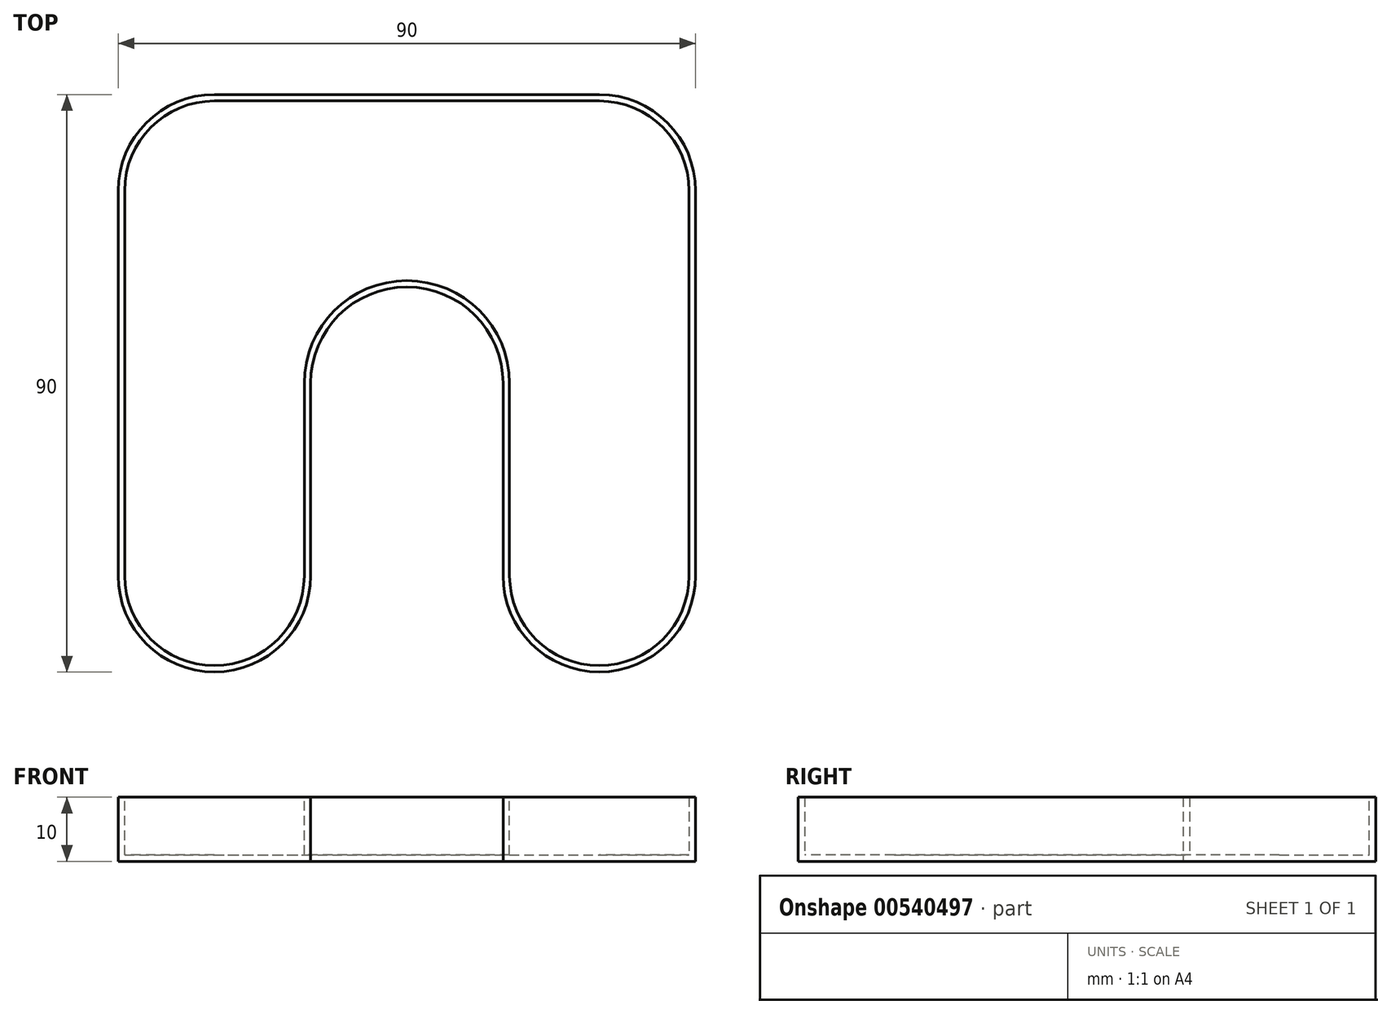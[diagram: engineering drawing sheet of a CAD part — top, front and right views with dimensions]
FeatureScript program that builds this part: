
annotation { "Feature Type Name" : "Feature", "Feature Type Description" : "" }
export const myFeature = defineFeature(function(context is Context, id is Id, definition is map)
    precondition{}
    {
        {
            var Q0;
            Q0=qCreatedBy(makeId("Top.planeOp"),FACE);
            var sketch = newSketch(context, id + "F0", { "sketchPlane" : qUnion([Q0])});
            skLineSegment(sketch, "E0", {"start": v(-29.25, 50.56) * mm, "end": v(30.75, 50.56) * mm});
            skLineSegment(sketch, "E1", {"start": v(45.75, 35.56) * mm, "end": v(45.75, -24.44) * mm});
            skLineSegment(sketch, "E2", {"start": v(30.75, -39.44) * mm, "end": v(30.75, -39.44) * mm});
            skLineSegment(sketch, "E3", {"start": v(15.75, -24.44) * mm, "end": v(15.75, 5.56) * mm});
            skLineSegment(sketch, "E4", {"start": v(0.75, 20.56) * mm, "end": v(0.75, 20.56) * mm});
            skLineSegment(sketch, "E5", {"start": v(-14.25, 5.56) * mm, "end": v(-14.25, -24.44) * mm});
            skLineSegment(sketch, "E6", {"start": v(-29.25, -39.44) * mm, "end": v(-29.25, -39.44) * mm});
            skLineSegment(sketch, "E7", {"start": v(-44.25, -24.44) * mm, "end": v(-44.25, 35.56) * mm});
            skPoint(sketch, "E8.visualSharp", {"position": v(-44.25, 50.56) * mm});
            skArc(sketch, "E8.filletArc", {"start": v(-29.25, 50.56) * mm, "mid": v(-39.86, 46.17) * mm, "end": v(-44.25, 35.56) * mm});
            skPoint(sketch, "E9.visualSharp", {"position": v(-14.25, 20.56) * mm});
            skArc(sketch, "E9.filletArc", {"start": v(0.75, 20.56) * mm, "mid": v(-9.86, 16.17) * mm, "end": v(-14.25, 5.56) * mm});
            skPoint(sketch, "E10.visualSharp", {"position": v(15.75, 20.56) * mm});
            skArc(sketch, "E10.filletArc", {"start": v(15.75, 5.56) * mm, "mid": v(11.35, 16.17) * mm, "end": v(0.75, 20.56) * mm});
            skPoint(sketch, "E11.visualSharp", {"position": v(45.75, 50.56) * mm});
            skArc(sketch, "E11.filletArc", {"start": v(45.75, 35.56) * mm, "mid": v(41.35, 46.17) * mm, "end": v(30.75, 50.56) * mm});
            skPoint(sketch, "E12.visualSharp", {"position": v(15.75, -39.44) * mm});
            skArc(sketch, "E12.filletArc", {"start": v(15.75, -24.44) * mm, "mid": v(20.14, -35.05) * mm, "end": v(30.75, -39.44) * mm});
            skPoint(sketch, "E13.visualSharp", {"position": v(45.75, -39.44) * mm});
            skArc(sketch, "E13.filletArc", {"start": v(30.75, -39.44) * mm, "mid": v(41.35, -35.05) * mm, "end": v(45.75, -24.44) * mm});
            skPoint(sketch, "E14.visualSharp", {"position": v(-14.25, -39.44) * mm});
            skArc(sketch, "E14.filletArc", {"start": v(-29.25, -39.44) * mm, "mid": v(-18.65, -35.05) * mm, "end": v(-14.25, -24.44) * mm});
            skPoint(sketch, "E15.visualSharp", {"position": v(-44.25, -39.44) * mm});
            skArc(sketch, "E15.filletArc", {"start": v(-44.25, -24.44) * mm, "mid": v(-39.86, -35.05) * mm, "end": v(-29.25, -39.44) * mm});
            skSolve(sketch);
        }
        {
            var Q0;
            Q0=makeQuery(id+"F0.imprint","IMPRINT",FACE,{"disambiguationData":[TD([[makeQuery(id+"F0.imprint","IMPRINT",EDGE,{"derivedFrom":sQuery(id+"F0.wireOp",EDGE,"E0")}),-1.0]])]});
            extrude(context, id + "F1", {"entities" : qUnion([Q0]), "depth" : 10 * mm, "offsetDistance" : 25 * mm});
        }
        {
            var Q0;
            Q0=makeQuery(id+"F1.opExtrude","CAP_FACE",FACE,{"disambiguationData":[OSD([sQuery(id+"F0.wireOp",EDGE,"E0"),sQuery(id+"F0.wireOp",EDGE,"E1"),sQuery(id+"F0.wireOp",EDGE,"E3"),sQuery(id+"F0.wireOp",EDGE,"E5"),sQuery(id+"F0.wireOp",EDGE,"E7"),sQuery(id+"F0.wireOp",EDGE,"E8.filletArc"),sQuery(id+"F0.wireOp",EDGE,"E9.filletArc"),sQuery(id+"F0.wireOp",EDGE,"E10.filletArc"),sQuery(id+"F0.wireOp",EDGE,"E11.filletArc"),sQuery(id+"F0.wireOp",EDGE,"E12.filletArc"),sQuery(id+"F0.wireOp",EDGE,"E13.filletArc"),sQuery(id+"F0.wireOp",EDGE,"E14.filletArc"),sQuery(id+"F0.wireOp",EDGE,"E15.filletArc")])],"isStart":false});
            shell(context, id + "F2", {"entities" : qUnion([Q0]), "thickness" : 1 * mm});
        }
    });
